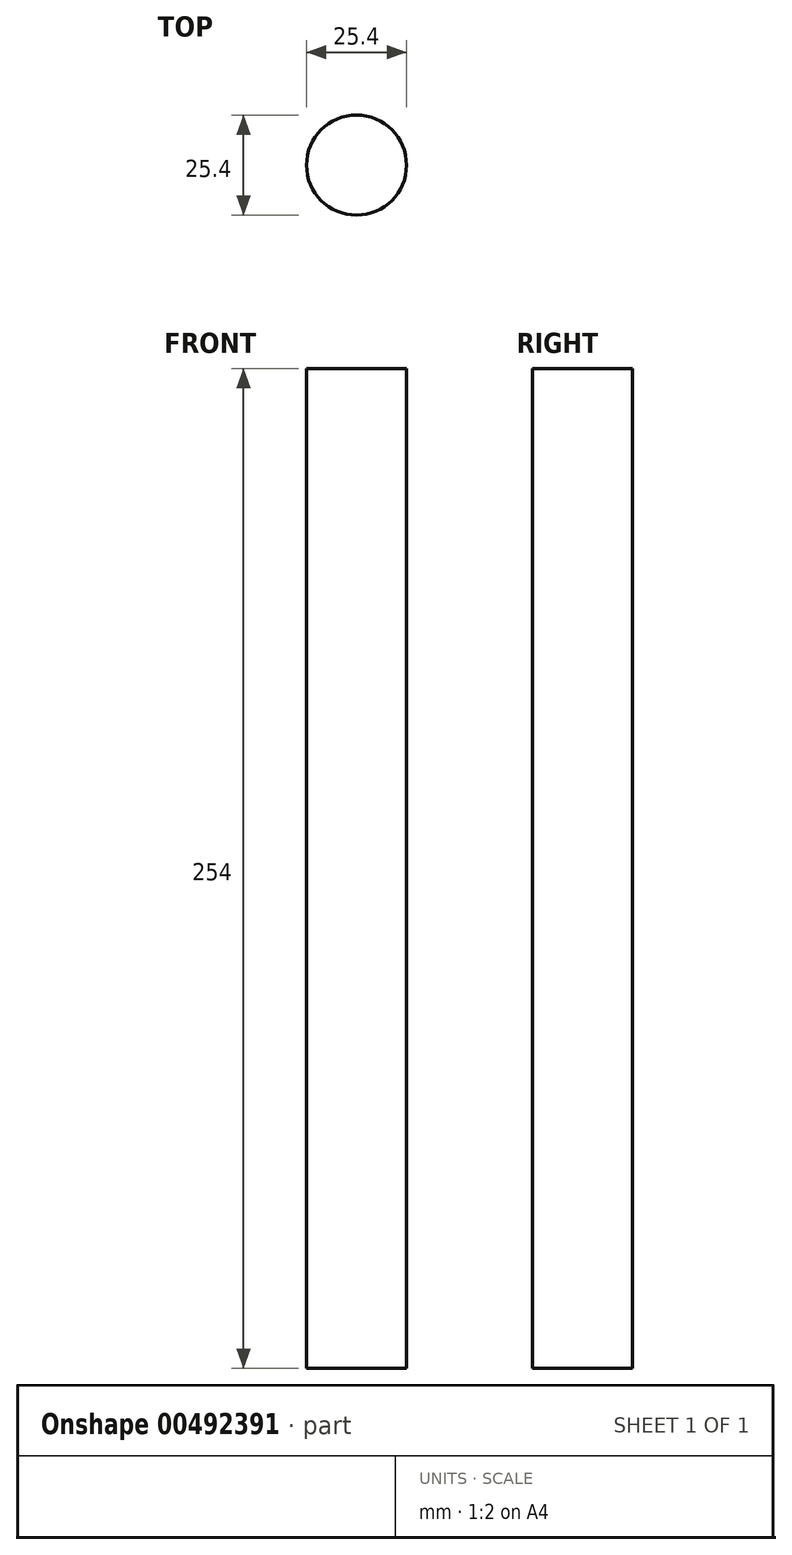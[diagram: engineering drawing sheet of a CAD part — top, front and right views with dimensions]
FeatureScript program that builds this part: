
annotation { "Feature Type Name" : "Feature", "Feature Type Description" : "" }
export const myFeature = defineFeature(function(context is Context, id is Id, definition is map)
    precondition{}
    {
        {
            var Q0;
            Q0=qCreatedBy(makeId("Top.planeOp"),FACE);
            var sketch = newSketch(context, id + "F0", { "sketchPlane" : qUnion([Q0])});
            skCircle(sketch, "E0", {"center": v(0, 0) * mm, "radius": 12.7 * mm});
            skSolve(sketch);
        }
        {
            var Q0;
            Q0=makeQuery(id+"F0.imprint","IMPRINT",FACE,{"disambiguationData":[TD([[makeQuery(id+"F0.imprint","IMPRINT",EDGE,{"derivedFrom":sQuery(id+"F0.wireOp",EDGE,"E0")}),1.0]])]});
            extrude(context, id + "F1", {"entities" : qUnion([Q0]), "depth" : 254 * mm});
        }
    });
